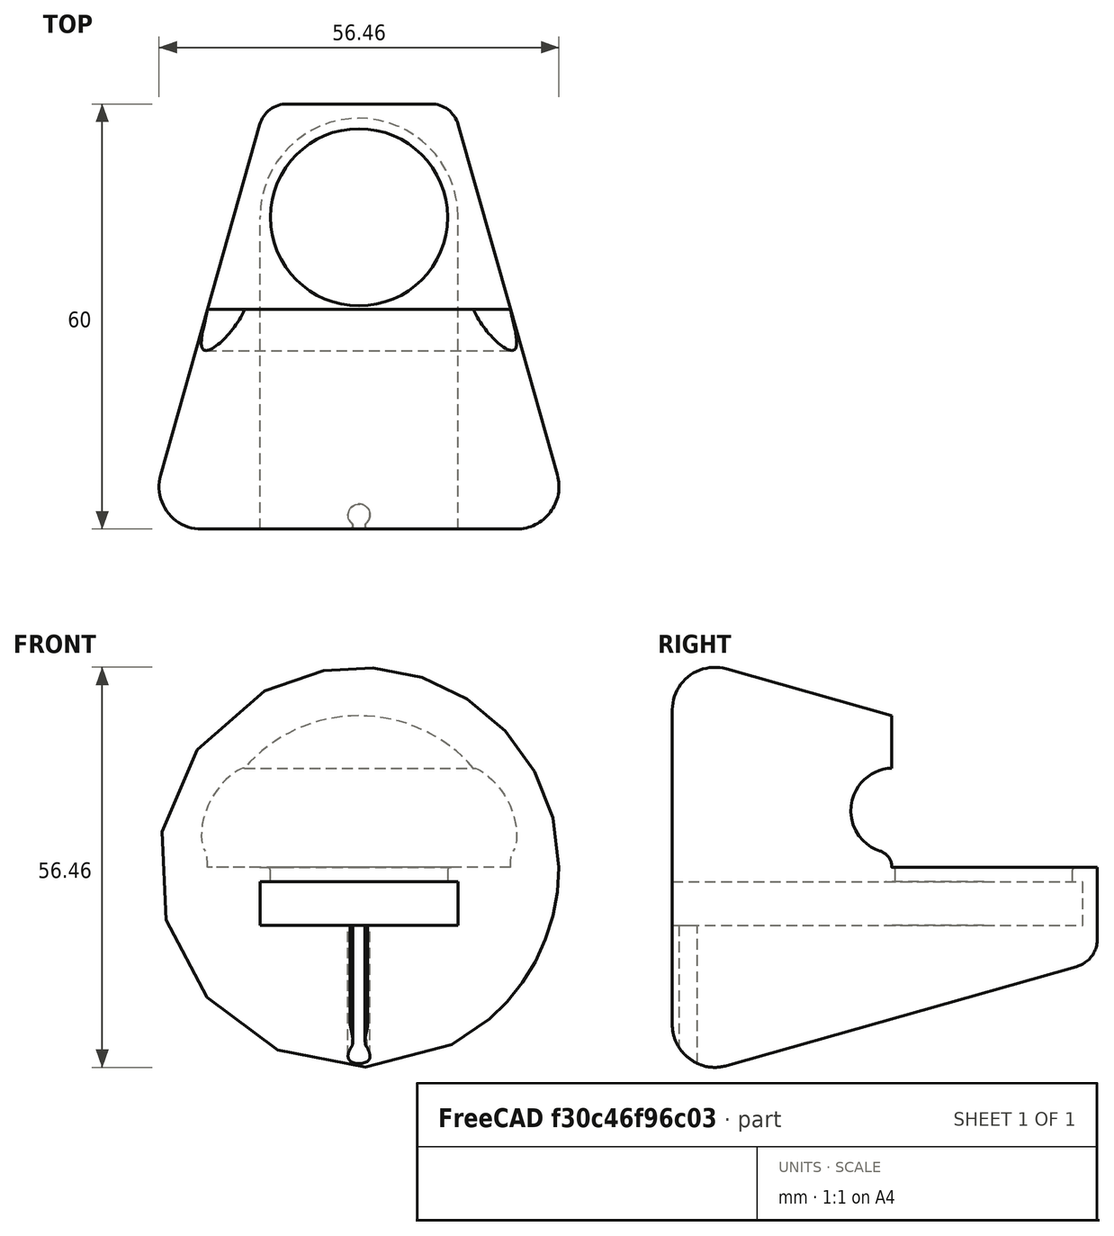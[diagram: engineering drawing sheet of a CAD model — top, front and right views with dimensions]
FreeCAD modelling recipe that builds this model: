
FCSTD DOCUMENT  (FreeCAD 0.20R29410 (Git))
Label: charging_stand
License: All rights reserved
LicenseURL: http://en.wikipedia.org/wiki/All_rights_reserved
objects: Sketcher::SketchObject×7, PartDesign::Pocket×6, PartDesign::Plane×4, PartDesign::Fillet×3, Mesh::Feature×2, PartDesign::Revolution×1, PartDesign::Body×1
note: 32 computed .brp shape members not serialized (recipe doc carries the construction recipe); baked Part::Feature solids carry a one-line shape summary decoded from their .brp

FEATURE [Sketcher::SketchObject] Sketch
  FullyConstrained = true
  MapMode = 5
  Support = -> [XY_Plane]
  sketch-geometry (6):
    g0: LineSegment StartX=0 StartY=0 StartZ=0 EndX=22.2269 EndY=0 EndZ=0
    g1: LineSegment StartX=28 StartY=7.63428 StartZ=0 EndX=14 EndY=57.0895 EndZ=0
    g2: LineSegment StartX=10.1512 StartY=60 StartZ=0 EndX=0 EndY=60 EndZ=0
    g3: LineSegment StartX=0 StartY=60 StartZ=0 EndX=0 EndY=0 EndZ=0
    g4: ArcOfCircle CenterX=10.1512 CenterY=56 CenterZ=0 NormalX=0 NormalY=0 NormalZ=1 AngleXU=0 Radius=4 StartAngle=0.275866 EndAngle=1.5708
    g5: ArcOfCircle CenterX=22.2269 CenterY=6 CenterZ=0 NormalX=0 NormalY=0 NormalZ=1 AngleXU=0 Radius=6 StartAngle=4.71239 EndAngle=6.55905
  constraints (15):
    c: Coincident(g-1,g0)
    c: Horizontal(g2)
    c: Coincident(g2,g3)
    c: Coincident(g3,g0)
    c: Vertical(g3)
    c: DistanceY(g3,g3) = 60
    c: Tangent(g2,g4) = -1.5708
    c: Tangent(g1,g4) = -1.5708
    c: DistanceX(g2,g1) = 14
    c: Radius(g4) = 4
    c: Tangent(g0,g5) = -1.5708
    c: Tangent(g1,g5) = -1.5708
    c: Horizontal(g0)
    c: Radius(g5) = 6
    c: DistanceX(g0,g1) = 28
FEATURE [PartDesign::Revolution] Revolution
  Angle = 360
  Axis = (0,1,0)
  Base = (0,0,0)
  Profile = -> Sketch
  ReferenceAxis = -> Sketch [V_Axis]
  Reversed = true
FEATURE [PartDesign::Plane] DatumPlane
  AttachmentOffset = pos=(0,0,0) rot=(0,1,0;1.5708rad)
  Length = 70.2477
  MapMode = 2
  Placement = pos=(0,0,0) rot=(0,1,0;1.5708rad)
  ResizeMode = 0
  Support = -> [Sketch]
  Width = 98.8477
FEATURE [Sketcher::SketchObject] Sketch001
  FullyConstrained = true
  MapMode = 5
  Placement = pos=(0,0,0) rot=(0,1,0;1.5708rad)
  Support = -> [DatumPlane]
  sketch-geometry (4):
    g0: LineSegment StartX=0 StartY=60 StartZ=0 EndX=-24 EndY=60 EndZ=0
    g1: LineSegment StartX=-24 StartY=60 StartZ=0 EndX=-24 EndY=31 EndZ=0
    g2: LineSegment StartX=-24 StartY=31 StartZ=0 EndX=0 EndY=31 EndZ=0
    g3: LineSegment StartX=0 StartY=31 StartZ=0 EndX=0 EndY=60 EndZ=0
  constraints (12):
    c: Coincident(g0,g1)
    c: Coincident(g1,g2)
    c: Coincident(g2,g3)
    c: Coincident(g3,g0)
    c: Horizontal(g0)
    c: Horizontal(g2)
    c: Vertical(g1)
    c: Vertical(g3)
    c: PointOnObject(g0,g-2)
    c: DistanceY(g1,g1) = 29
    c: DistanceX(g0,g0) = 24
    c: DistanceY(g0) = 60
FEATURE [PartDesign::Pocket] Pocket
  BaseFeature = -> Revolution
  Direction = (-1,0,-2e-16)
  Length = 50
  Length2 = 50
  Profile = -> Sketch001
  ReferenceAxis = -> Sketch001 [N_Axis]
  Type = 4
FEATURE [PartDesign::Plane] DatumPlane001
  AttachmentOffset = pos=(0,0,-2) rot=(0,0,1;0rad)
  Length = 70.1318
  MapMode = 5
  Placement = pos=(4e-16,0,-2) rot=(0,0,1;0rad)
  ResizeMode = 0
  Support = -> [Pocket]
  Width = 98.8351
FEATURE [Sketcher::SketchObject] Sketch002
  FullyConstrained = true
  MapMode = 5
  Placement = pos=(4e-16,0,-2) rot=(0,0,1;0rad)
  Support = -> [DatumPlane001]
  sketch-geometry (1):
    g0: Circle CenterX=0 CenterY=44 CenterZ=0 NormalX=0 NormalY=0 NormalZ=1 AngleXU=0 Radius=13.975
  constraints (3):
    c: PointOnObject(g0,g-2)
    c: Diameter(g0) = 27.95
    c: DistanceY(g0) = 44
FEATURE [PartDesign::Pocket] Pocket001
  BaseFeature = -> Pocket
  Direction = (2e-16,0,-1)
  Length = 6.2
  Length2 = 5
  Profile = -> Sketch002
  ReferenceAxis = -> Sketch002 [N_Axis]
  Type = 0
FEATURE [Sketcher::SketchObject] Sketch003
  FullyConstrained = true
  MapMode = 5
  Support = -> [Pocket001]
  sketch-geometry (1):
    g0: Circle CenterX=0 CenterY=44 CenterZ=0 NormalX=0 NormalY=0 NormalZ=1 AngleXU=0 Radius=12.5
  constraints (3):
    c: PointOnObject(g0,g-2)
    c: Diameter(g0) = 25
    c: DistanceY(g0) = 44
FEATURE [PartDesign::Pocket] Pocket002
  BaseFeature = -> Pocket001
  Direction = (2e-16,0,-1)
  Length = 5
  Length2 = 5
  Profile = -> Sketch003
  ReferenceAxis = -> Sketch003 [N_Axis]
  Type = 0
FEATURE [PartDesign::Plane] DatumPlane002
  AttachmentOffset = pos=(0,0,0) rot=(0,1,0;1.5708rad)
  Length = 70.2477
  MapMode = 5
  Placement = pos=(0,0,0) rot=(0,1,0;1.5708rad)
  ResizeMode = 0
  Support = -> [Pocket002]
  Width = 98.8477
FEATURE [Sketcher::SketchObject] Sketch004
  FullyConstrained = true
  MapMode = 5
  Placement = pos=(0,0,0) rot=(0,1,0;1.5708rad)
  Support = -> [DatumPlane002]
  sketch-geometry (4):
    g0: ArcOfCircle CenterX=-8 CenterY=31.2 CenterZ=0 NormalX=0 NormalY=0 NormalZ=1 AngleXU=0 Radius=6 StartAngle=3.14159 EndAngle=6.28319
    g1: LineSegment StartX=-14 StartY=31.2 StartZ=0 EndX=-14 EndY=47.2 EndZ=0
    g2: LineSegment StartX=-14 StartY=47.2 StartZ=0 EndX=-2 EndY=47.2 EndZ=0
    g3: LineSegment StartX=-2 StartY=47.2 StartZ=0 EndX=-2 EndY=31.2 EndZ=0
  constraints (12):
    c: Radius(g0) = 6
    c: DistanceY(g0) = 31.2
    c: DistanceX(g0,g-1) = 2
    c: Tangent(g0,g1) = 1.5708
    c: Coincident(g1,g2)
    c: Horizontal(g2)
    c: Coincident(g2,g3)
    c: Coincident(g3,g0)
    c: Vertical(g3)
    c: DistanceX(g1,g2) = 12
    c: DistanceY(g0,g1) = 16
    c: Horizontal(g0,g0)
FEATURE [PartDesign::Pocket] Pocket003
  BaseFeature = -> Pocket002
  Direction = (-1,0,-4e-16)
  Length = 40
  Length2 = 40
  Profile = -> Sketch004
  ReferenceAxis = -> Sketch004 [N_Axis]
  Type = 4
FEATURE [Sketcher::SketchObject] Sketch005
  FullyConstrained = true
  MapMode = 5
  Placement = pos=(0,0,0) rot=(1,0,0;1.5708rad)
  sketch-geometry (4):
    g0: LineSegment StartX=13.975 StartY=-8.2 StartZ=0 EndX=-13.975 EndY=-8.2 EndZ=0
    g1: LineSegment StartX=-13.975 StartY=-8.2 StartZ=0 EndX=-13.975 EndY=-2 EndZ=0
    g2: LineSegment StartX=-13.975 StartY=-2 StartZ=0 EndX=13.975 EndY=-2 EndZ=0
    g3: LineSegment StartX=13.975 StartY=-2 StartZ=0 EndX=13.975 EndY=-8.2 EndZ=0
  constraints (11):
    c: Coincident(g0,g1)
    c: Coincident(g1,g2)
    c: Coincident(g2,g3)
    c: Coincident(g3,g0)
    c: Horizontal(g0)
    c: Vertical(g1)
    c: Vertical(g3)
    c: Symmetric(g2,g1,g-2)
    c: DistanceY(g0,g2) = 6.2
    c: DistanceX(g0,g0) = 27.95
    c: DistanceY(g2,g-1) = 2
FEATURE [PartDesign::Pocket] Pocket004
  BaseFeature = -> Pocket003
  Direction = (0,1,-2e-16)
  Length = 44
  Length2 = 5
  Profile = -> Sketch005
  ReferenceAxis = -> Sketch005 [N_Axis]
  Type = 0
FEATURE [Mesh::Feature] Mesh  label="xp1_mesh"
FEATURE [PartDesign::Plane] DatumPlane003
  Length = 70.1318
  MapMode = 5
  Placement = pos=(0,-1.8e-15,-8.2) rot=(0,0,1;0rad)
  ResizeMode = 0
  Support = -> [Pocket004]
  Width = 98.8351
FEATURE [Sketcher::SketchObject] Sketch006
  FullyConstrained = true
  MapMode = 5
  Placement = pos=(0,-1.8e-15,-8.2) rot=(0,0,1;0rad)
  Support = -> [DatumPlane003]
  sketch-geometry (6):
    g0: ArcOfCircle CenterX=0 CenterY=2 CenterZ=0 NormalX=0 NormalY=0 NormalZ=1 AngleXU=0 Radius=1.55 StartAngle=5.49415 EndAngle=10.2138
    g1: ArcOfCircle CenterX=-1.36589 CenterY=0.481679 CenterZ=0 NormalX=0 NormalY=0 NormalZ=1 AngleXU=0 Radius=0.5 StartAngle=4.44085 EndAngle=7.27431
    g2: ArcOfCircle CenterX=1.36589 CenterY=0.481679 CenterZ=0 NormalX=0 NormalY=0 NormalZ=1 AngleXU=0 Radius=0.5 StartAngle=2.15047 EndAngle=4.98393
    g3: LineSegment StartX=-1.5 StartY=4.1158e-12 StartZ=0 EndX=-1.5 EndY=-0.5 EndZ=0
    g4: LineSegment StartX=-1.5 StartY=-0.5 StartZ=0 EndX=1.5 EndY=-0.5 EndZ=0
    g5: LineSegment StartX=1.5 StartY=-0.5 StartZ=0 EndX=1.5 EndY=4.1158e-12 EndZ=0
  constraints (20):
    c: PointOnObject(g0,g-2)
    c: Radius(g0) = 1.55
    c: DistanceY(g0) = 2
    c: Coincident(g1,g0)
    c: PointOnObject(g1,g-1)
    c: Coincident(g2,g0)
    c: Symmetric(g2,g1,g-2)
    c: Horizontal(g0,g0)
    c: DistanceX(g1,g2) = 3
    c: Radius(g1) = 0.5
    c: Radius(g2) = 0.5
    c: Coincident(g3,g1)
    c: Vertical(g3)
    c: Coincident(g4,g3)
    c: Horizontal(g4)
    c: Coincident(g5,g2)
    c: Vertical(g5)
    c: Coincident(g4,g5)
    c: DistanceY(g3) = -0.5
    c: DistanceY(g0) = 0.9
FEATURE [PartDesign::Pocket] Pocket005
  BaseFeature = -> Pocket004
  Direction = (0,-2e-16,-1)
  Length = 25
  Length2 = 5
  Profile = -> Sketch006
  ReferenceAxis = -> Sketch006 [N_Axis]
  Type = 0
FEATURE [PartDesign::Fillet] Fillet001
  Base = -> Pocket005 [Edge52]
  BaseFeature = -> Pocket005
  Radius = 2.4
  SupportTransform = false
  UseAllEdges = false
FEATURE [PartDesign::Fillet] Fillet002
  Base = -> Fillet001 [Edge30]
  BaseFeature = -> Fillet001
  Radius = 0.5
  SupportTransform = false
  UseAllEdges = false
FEATURE [PartDesign::Fillet] Fillet
  Base = -> Pocket005 [Edge23]
  BaseFeature = -> Pocket005
  Radius = 0.25
  SupportTransform = false
  UseAllEdges = false
FEATURE [PartDesign::Body] Body  label="main_body"
  Group = -> [Sketch,Revolution,DatumPlane,Sketch001,Pocket,DatumPlane001,Sketch002,Pocket001,Sketch003,Pocket002,DatumPlane002,Sketch004,Pocket003,Sketch005,Pocket004,DatumPlane003,Sketch006,Pocket005,Fillet,Fillet001,Fillet002]
  Origin = -> Origin
  Tip = -> Fillet002
FEATURE [Mesh::Feature] Mesh001  label="xp2_mesh"
